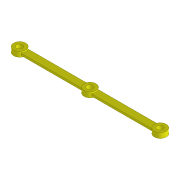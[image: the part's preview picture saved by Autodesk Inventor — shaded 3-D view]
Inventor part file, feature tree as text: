
AUTODESK INVENTOR PART (.ipt)
format: ipt  version: 2017 (Build 210142000, 142)  size: 120,832 bytes
history: native  units: mm
features: extrude x4, sketch x4, projected_geometry x2, mirror x1
ambient origin geometry x8: Origin, YZ Plane, XZ Plane, XY Plane, X Axis, Y Axis, Z Axis, Center Point
bodies: Solid1 (feature_tree)
feature tree (11):
  extrude  "Extrusion1"  Depth=6.0mm
  extrude  "Extrusion2"  Depth=7.0mm
  mirror  "Mirror1"
  extrude  "Extrusion3"  Depth=1.5mm TaperAngle=0.0deg
  extrude  "Extrusion4"  Depth=5.0mm TaperAngle=0.0deg
  sketch  "Sketch1"  dims[d0=140.0mm d1=6.0mm]
  sketch  "Sketch2"  dims[d2=12.0mm d3=7.0mm]
  sketch  "Sketch3"  dims[d4=5.0mm d5=0.0mm d6=1.5mm d7=0.0mm]
  projected_geometry  "Projected Loop1"
  sketch  "Sketch4"  dims[d8=12.0mm d9=5.0mm d10=0.0mm d11=6.0mm d12=5.0mm d13=0.0mm]
  projected_geometry  "Projected Loop2"
